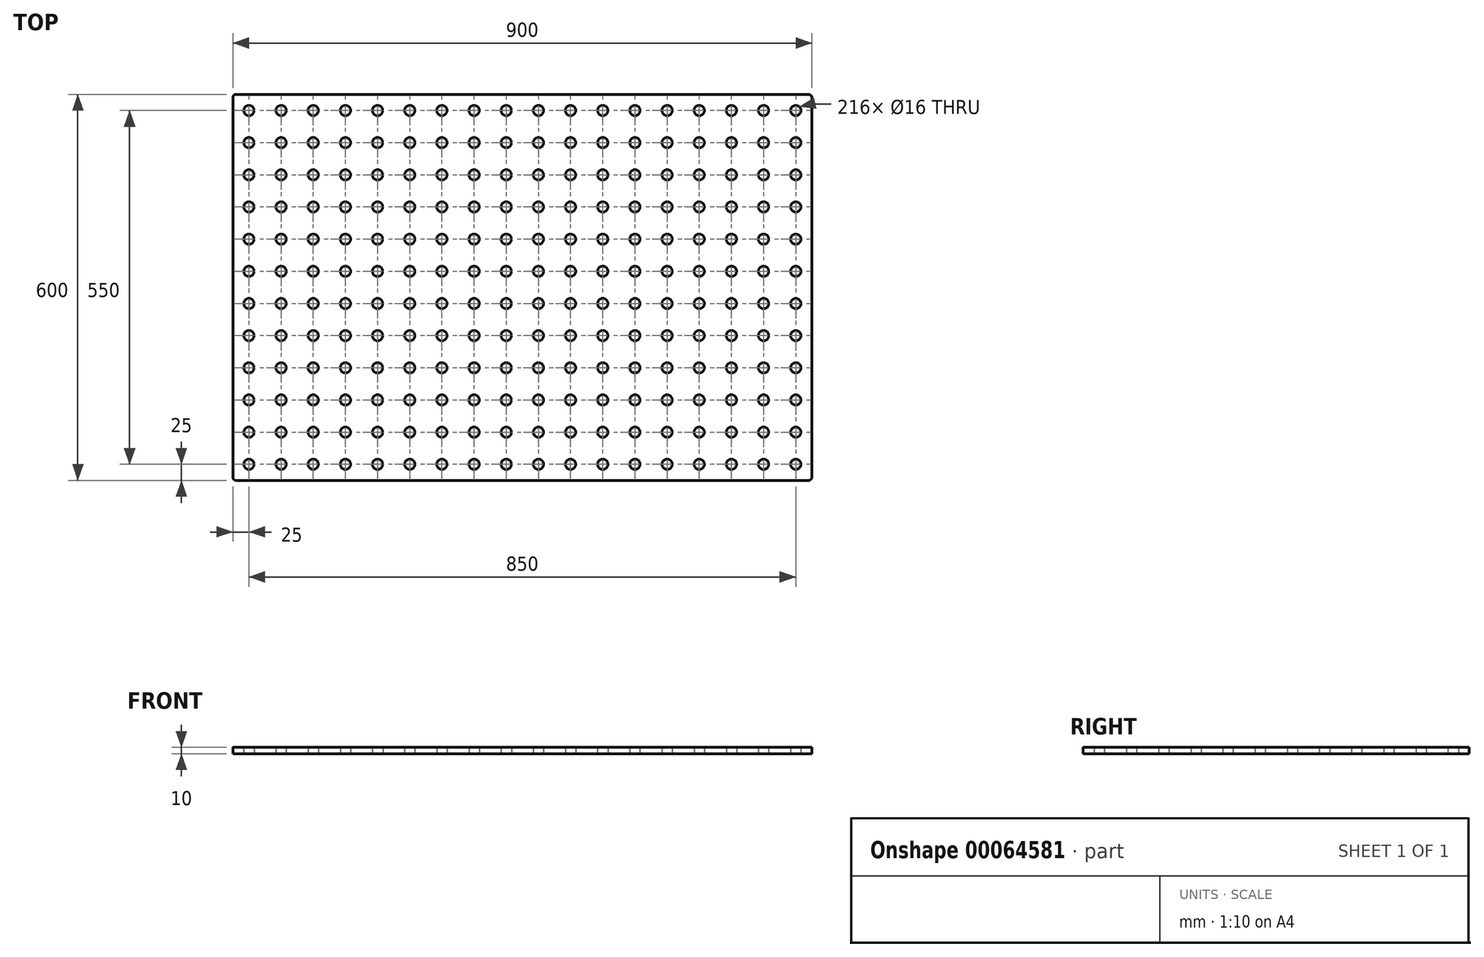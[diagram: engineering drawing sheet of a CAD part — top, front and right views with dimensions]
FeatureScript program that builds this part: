
annotation { "Feature Type Name" : "Feature", "Feature Type Description" : "" }
export const myFeature = defineFeature(function(context is Context, id is Id, definition is map)
    precondition{}
    {
        {
            var Q0;
            Q0=qCreatedBy(makeId("Top.planeOp"),FACE);
            var sketch = newSketch(context, id + "F0", { "sketchPlane" : qUnion([Q0])});
            skLineSegment(sketch, "E0.bottom", {"start": v(5, 0) * mm, "end": v(895, 0) * mm});
            skLineSegment(sketch, "E0.top", {"start": v(5, 600) * mm, "end": v(895, 600) * mm});
            skLineSegment(sketch, "E0.left", {"start": v(0, 5) * mm, "end": v(0, 595) * mm});
            skLineSegment(sketch, "E0.right", {"start": v(900, 5) * mm, "end": v(900, 595) * mm});
            skCircle(sketch, "E1", {"center": v(25, 575) * mm, "radius": 8 * mm});
            skCircle(sketch, "E2.0.1.0", {"center": v(25, 525) * mm, "radius": 8 * mm});
            skCircle(sketch, "E2.0.2.0", {"center": v(25, 475) * mm, "radius": 8 * mm});
            skCircle(sketch, "E2.0.3.0", {"center": v(25, 425) * mm, "radius": 8 * mm});
            skCircle(sketch, "E2.0.4.0", {"center": v(25, 375) * mm, "radius": 8 * mm});
            skCircle(sketch, "E2.0.5.0", {"center": v(25, 325) * mm, "radius": 8 * mm});
            skCircle(sketch, "E2.0.6.0", {"center": v(25, 275) * mm, "radius": 8 * mm});
            skCircle(sketch, "E2.0.7.0", {"center": v(25, 225) * mm, "radius": 8 * mm});
            skCircle(sketch, "E2.0.8.0", {"center": v(25, 175) * mm, "radius": 8 * mm});
            skCircle(sketch, "E2.0.9.0", {"center": v(25, 125) * mm, "radius": 8 * mm});
            skCircle(sketch, "E2.0.10.0", {"center": v(25, 75) * mm, "radius": 8 * mm});
            skCircle(sketch, "E2.0.11.0", {"center": v(25, 25) * mm, "radius": 8 * mm});
            skCircle(sketch, "E2.1.0.0", {"center": v(75, 575) * mm, "radius": 8 * mm});
            skCircle(sketch, "E2.1.1.0", {"center": v(75, 525) * mm, "radius": 8 * mm});
            skCircle(sketch, "E2.1.2.0", {"center": v(75, 475) * mm, "radius": 8 * mm});
            skCircle(sketch, "E2.1.3.0", {"center": v(75, 425) * mm, "radius": 8 * mm});
            skCircle(sketch, "E2.1.4.0", {"center": v(75, 375) * mm, "radius": 8 * mm});
            skCircle(sketch, "E2.1.5.0", {"center": v(75, 325) * mm, "radius": 8 * mm});
            skCircle(sketch, "E2.1.6.0", {"center": v(75, 275) * mm, "radius": 8 * mm});
            skCircle(sketch, "E2.1.7.0", {"center": v(75, 225) * mm, "radius": 8 * mm});
            skCircle(sketch, "E2.1.8.0", {"center": v(75, 175) * mm, "radius": 8 * mm});
            skCircle(sketch, "E2.1.9.0", {"center": v(75, 125) * mm, "radius": 8 * mm});
            skCircle(sketch, "E2.1.10.0", {"center": v(75, 75) * mm, "radius": 8 * mm});
            skCircle(sketch, "E2.1.11.0", {"center": v(75, 25) * mm, "radius": 8 * mm});
            skCircle(sketch, "E2.2.0.0", {"center": v(125, 575) * mm, "radius": 8 * mm});
            skCircle(sketch, "E2.2.1.0", {"center": v(125, 525) * mm, "radius": 8 * mm});
            skCircle(sketch, "E2.2.2.0", {"center": v(125, 475) * mm, "radius": 8 * mm});
            skCircle(sketch, "E2.2.3.0", {"center": v(125, 425) * mm, "radius": 8 * mm});
            skCircle(sketch, "E2.2.4.0", {"center": v(125, 375) * mm, "radius": 8 * mm});
            skCircle(sketch, "E2.2.5.0", {"center": v(125, 325) * mm, "radius": 8 * mm});
            skCircle(sketch, "E2.2.6.0", {"center": v(125, 275) * mm, "radius": 8 * mm});
            skCircle(sketch, "E2.2.7.0", {"center": v(125, 225) * mm, "radius": 8 * mm});
            skCircle(sketch, "E2.2.8.0", {"center": v(125, 175) * mm, "radius": 8 * mm});
            skCircle(sketch, "E2.2.9.0", {"center": v(125, 125) * mm, "radius": 8 * mm});
            skCircle(sketch, "E2.2.10.0", {"center": v(125, 75) * mm, "radius": 8 * mm});
            skCircle(sketch, "E2.2.11.0", {"center": v(125, 25) * mm, "radius": 8 * mm});
            skCircle(sketch, "E2.3.0.0", {"center": v(175, 575) * mm, "radius": 8 * mm});
            skCircle(sketch, "E2.3.1.0", {"center": v(175, 525) * mm, "radius": 8 * mm});
            skCircle(sketch, "E2.3.2.0", {"center": v(175, 475) * mm, "radius": 8 * mm});
            skCircle(sketch, "E2.3.3.0", {"center": v(175, 425) * mm, "radius": 8 * mm});
            skCircle(sketch, "E2.3.4.0", {"center": v(175, 375) * mm, "radius": 8 * mm});
            skCircle(sketch, "E2.3.5.0", {"center": v(175, 325) * mm, "radius": 8 * mm});
            skCircle(sketch, "E2.3.6.0", {"center": v(175, 275) * mm, "radius": 8 * mm});
            skCircle(sketch, "E2.3.7.0", {"center": v(175, 225) * mm, "radius": 8 * mm});
            skCircle(sketch, "E2.3.8.0", {"center": v(175, 175) * mm, "radius": 8 * mm});
            skCircle(sketch, "E2.3.9.0", {"center": v(175, 125) * mm, "radius": 8 * mm});
            skCircle(sketch, "E2.3.10.0", {"center": v(175, 75) * mm, "radius": 8 * mm});
            skCircle(sketch, "E2.3.11.0", {"center": v(175, 25) * mm, "radius": 8 * mm});
            skCircle(sketch, "E2.4.0.0", {"center": v(225, 575) * mm, "radius": 8 * mm});
            skCircle(sketch, "E2.4.1.0", {"center": v(225, 525) * mm, "radius": 8 * mm});
            skCircle(sketch, "E2.4.2.0", {"center": v(225, 475) * mm, "radius": 8 * mm});
            skCircle(sketch, "E2.4.3.0", {"center": v(225, 425) * mm, "radius": 8 * mm});
            skCircle(sketch, "E2.4.4.0", {"center": v(225, 375) * mm, "radius": 8 * mm});
            skCircle(sketch, "E2.4.5.0", {"center": v(225, 325) * mm, "radius": 8 * mm});
            skCircle(sketch, "E2.4.6.0", {"center": v(225, 275) * mm, "radius": 8 * mm});
            skCircle(sketch, "E2.4.7.0", {"center": v(225, 225) * mm, "radius": 8 * mm});
            skCircle(sketch, "E2.4.8.0", {"center": v(225, 175) * mm, "radius": 8 * mm});
            skCircle(sketch, "E2.4.9.0", {"center": v(225, 125) * mm, "radius": 8 * mm});
            skCircle(sketch, "E2.4.10.0", {"center": v(225, 75) * mm, "radius": 8 * mm});
            skCircle(sketch, "E2.4.11.0", {"center": v(225, 25) * mm, "radius": 8 * mm});
            skCircle(sketch, "E2.5.0.0", {"center": v(275, 575) * mm, "radius": 8 * mm});
            skCircle(sketch, "E2.5.1.0", {"center": v(275, 525) * mm, "radius": 8 * mm});
            skCircle(sketch, "E2.5.2.0", {"center": v(275, 475) * mm, "radius": 8 * mm});
            skCircle(sketch, "E2.5.3.0", {"center": v(275, 425) * mm, "radius": 8 * mm});
            skCircle(sketch, "E2.5.4.0", {"center": v(275, 375) * mm, "radius": 8 * mm});
            skCircle(sketch, "E2.5.5.0", {"center": v(275, 325) * mm, "radius": 8 * mm});
            skCircle(sketch, "E2.5.6.0", {"center": v(275, 275) * mm, "radius": 8 * mm});
            skCircle(sketch, "E2.5.7.0", {"center": v(275, 225) * mm, "radius": 8 * mm});
            skCircle(sketch, "E2.5.8.0", {"center": v(275, 175) * mm, "radius": 8 * mm});
            skCircle(sketch, "E2.5.9.0", {"center": v(275, 125) * mm, "radius": 8 * mm});
            skCircle(sketch, "E2.5.10.0", {"center": v(275, 75) * mm, "radius": 8 * mm});
            skCircle(sketch, "E2.5.11.0", {"center": v(275, 25) * mm, "radius": 8 * mm});
            skCircle(sketch, "E2.6.0.0", {"center": v(325, 575) * mm, "radius": 8 * mm});
            skCircle(sketch, "E2.6.1.0", {"center": v(325, 525) * mm, "radius": 8 * mm});
            skCircle(sketch, "E2.6.2.0", {"center": v(325, 475) * mm, "radius": 8 * mm});
            skCircle(sketch, "E2.6.3.0", {"center": v(325, 425) * mm, "radius": 8 * mm});
            skCircle(sketch, "E2.6.4.0", {"center": v(325, 375) * mm, "radius": 8 * mm});
            skCircle(sketch, "E2.6.5.0", {"center": v(325, 325) * mm, "radius": 8 * mm});
            skCircle(sketch, "E2.6.6.0", {"center": v(325, 275) * mm, "radius": 8 * mm});
            skCircle(sketch, "E2.6.7.0", {"center": v(325, 225) * mm, "radius": 8 * mm});
            skCircle(sketch, "E2.6.8.0", {"center": v(325, 175) * mm, "radius": 8 * mm});
            skCircle(sketch, "E2.6.9.0", {"center": v(325, 125) * mm, "radius": 8 * mm});
            skCircle(sketch, "E2.6.10.0", {"center": v(325, 75) * mm, "radius": 8 * mm});
            skCircle(sketch, "E2.6.11.0", {"center": v(325, 25) * mm, "radius": 8 * mm});
            skCircle(sketch, "E2.7.0.0", {"center": v(375, 575) * mm, "radius": 8 * mm});
            skCircle(sketch, "E2.7.1.0", {"center": v(375, 525) * mm, "radius": 8 * mm});
            skCircle(sketch, "E2.7.2.0", {"center": v(375, 475) * mm, "radius": 8 * mm});
            skCircle(sketch, "E2.7.3.0", {"center": v(375, 425) * mm, "radius": 8 * mm});
            skCircle(sketch, "E2.7.4.0", {"center": v(375, 375) * mm, "radius": 8 * mm});
            skCircle(sketch, "E2.7.5.0", {"center": v(375, 325) * mm, "radius": 8 * mm});
            skCircle(sketch, "E2.7.6.0", {"center": v(375, 275) * mm, "radius": 8 * mm});
            skCircle(sketch, "E2.7.7.0", {"center": v(375, 225) * mm, "radius": 8 * mm});
            skCircle(sketch, "E2.7.8.0", {"center": v(375, 175) * mm, "radius": 8 * mm});
            skCircle(sketch, "E2.7.9.0", {"center": v(375, 125) * mm, "radius": 8 * mm});
            skCircle(sketch, "E2.7.10.0", {"center": v(375, 75) * mm, "radius": 8 * mm});
            skCircle(sketch, "E2.7.11.0", {"center": v(375, 25) * mm, "radius": 8 * mm});
            skCircle(sketch, "E2.8.0.0", {"center": v(425, 575) * mm, "radius": 8 * mm});
            skCircle(sketch, "E2.8.1.0", {"center": v(425, 525) * mm, "radius": 8 * mm});
            skCircle(sketch, "E2.8.2.0", {"center": v(425, 475) * mm, "radius": 8 * mm});
            skCircle(sketch, "E2.8.3.0", {"center": v(425, 425) * mm, "radius": 8 * mm});
            skCircle(sketch, "E2.8.4.0", {"center": v(425, 375) * mm, "radius": 8 * mm});
            skCircle(sketch, "E2.8.5.0", {"center": v(425, 325) * mm, "radius": 8 * mm});
            skCircle(sketch, "E2.8.6.0", {"center": v(425, 275) * mm, "radius": 8 * mm});
            skCircle(sketch, "E2.8.7.0", {"center": v(425, 225) * mm, "radius": 8 * mm});
            skCircle(sketch, "E2.8.8.0", {"center": v(425, 175) * mm, "radius": 8 * mm});
            skCircle(sketch, "E2.8.9.0", {"center": v(425, 125) * mm, "radius": 8 * mm});
            skCircle(sketch, "E2.8.10.0", {"center": v(425, 75) * mm, "radius": 8 * mm});
            skCircle(sketch, "E2.8.11.0", {"center": v(425, 25) * mm, "radius": 8 * mm});
            skCircle(sketch, "E2.9.0.0", {"center": v(475, 575) * mm, "radius": 8 * mm});
            skCircle(sketch, "E2.9.1.0", {"center": v(475, 525) * mm, "radius": 8 * mm});
            skCircle(sketch, "E2.9.2.0", {"center": v(475, 475) * mm, "radius": 8 * mm});
            skCircle(sketch, "E2.9.3.0", {"center": v(475, 425) * mm, "radius": 8 * mm});
            skCircle(sketch, "E2.9.4.0", {"center": v(475, 375) * mm, "radius": 8 * mm});
            skCircle(sketch, "E2.9.5.0", {"center": v(475, 325) * mm, "radius": 8 * mm});
            skCircle(sketch, "E2.9.6.0", {"center": v(475, 275) * mm, "radius": 8 * mm});
            skCircle(sketch, "E2.9.7.0", {"center": v(475, 225) * mm, "radius": 8 * mm});
            skCircle(sketch, "E2.9.8.0", {"center": v(475, 175) * mm, "radius": 8 * mm});
            skCircle(sketch, "E2.9.9.0", {"center": v(475, 125) * mm, "radius": 8 * mm});
            skCircle(sketch, "E2.9.10.0", {"center": v(475, 75) * mm, "radius": 8 * mm});
            skCircle(sketch, "E2.9.11.0", {"center": v(475, 25) * mm, "radius": 8 * mm});
            skCircle(sketch, "E2.10.0.0", {"center": v(525, 575) * mm, "radius": 8 * mm});
            skCircle(sketch, "E2.10.1.0", {"center": v(525, 525) * mm, "radius": 8 * mm});
            skCircle(sketch, "E2.10.2.0", {"center": v(525, 475) * mm, "radius": 8 * mm});
            skCircle(sketch, "E2.10.3.0", {"center": v(525, 425) * mm, "radius": 8 * mm});
            skCircle(sketch, "E2.10.4.0", {"center": v(525, 375) * mm, "radius": 8 * mm});
            skCircle(sketch, "E2.10.5.0", {"center": v(525, 325) * mm, "radius": 8 * mm});
            skCircle(sketch, "E2.10.6.0", {"center": v(525, 275) * mm, "radius": 8 * mm});
            skCircle(sketch, "E2.10.7.0", {"center": v(525, 225) * mm, "radius": 8 * mm});
            skCircle(sketch, "E2.10.8.0", {"center": v(525, 175) * mm, "radius": 8 * mm});
            skCircle(sketch, "E2.10.9.0", {"center": v(525, 125) * mm, "radius": 8 * mm});
            skCircle(sketch, "E2.10.10.0", {"center": v(525, 75) * mm, "radius": 8 * mm});
            skCircle(sketch, "E2.10.11.0", {"center": v(525, 25) * mm, "radius": 8 * mm});
            skCircle(sketch, "E2.11.0.0", {"center": v(575, 575) * mm, "radius": 8 * mm});
            skCircle(sketch, "E2.11.1.0", {"center": v(575, 525) * mm, "radius": 8 * mm});
            skCircle(sketch, "E2.11.2.0", {"center": v(575, 475) * mm, "radius": 8 * mm});
            skCircle(sketch, "E2.11.3.0", {"center": v(575, 425) * mm, "radius": 8 * mm});
            skCircle(sketch, "E2.11.4.0", {"center": v(575, 375) * mm, "radius": 8 * mm});
            skCircle(sketch, "E2.11.5.0", {"center": v(575, 325) * mm, "radius": 8 * mm});
            skCircle(sketch, "E2.11.6.0", {"center": v(575, 275) * mm, "radius": 8 * mm});
            skCircle(sketch, "E2.11.7.0", {"center": v(575, 225) * mm, "radius": 8 * mm});
            skCircle(sketch, "E2.11.8.0", {"center": v(575, 175) * mm, "radius": 8 * mm});
            skCircle(sketch, "E2.11.9.0", {"center": v(575, 125) * mm, "radius": 8 * mm});
            skCircle(sketch, "E2.11.10.0", {"center": v(575, 75) * mm, "radius": 8 * mm});
            skCircle(sketch, "E2.11.11.0", {"center": v(575, 25) * mm, "radius": 8 * mm});
            skCircle(sketch, "E2.12.0.0", {"center": v(625, 575) * mm, "radius": 8 * mm});
            skCircle(sketch, "E2.12.1.0", {"center": v(625, 525) * mm, "radius": 8 * mm});
            skCircle(sketch, "E2.12.2.0", {"center": v(625, 475) * mm, "radius": 8 * mm});
            skCircle(sketch, "E2.12.3.0", {"center": v(625, 425) * mm, "radius": 8 * mm});
            skCircle(sketch, "E2.12.4.0", {"center": v(625, 375) * mm, "radius": 8 * mm});
            skCircle(sketch, "E2.12.5.0", {"center": v(625, 325) * mm, "radius": 8 * mm});
            skCircle(sketch, "E2.12.6.0", {"center": v(625, 275) * mm, "radius": 8 * mm});
            skCircle(sketch, "E2.12.7.0", {"center": v(625, 225) * mm, "radius": 8 * mm});
            skCircle(sketch, "E2.12.8.0", {"center": v(625, 175) * mm, "radius": 8 * mm});
            skCircle(sketch, "E2.12.9.0", {"center": v(625, 125) * mm, "radius": 8 * mm});
            skCircle(sketch, "E2.12.10.0", {"center": v(625, 75) * mm, "radius": 8 * mm});
            skCircle(sketch, "E2.12.11.0", {"center": v(625, 25) * mm, "radius": 8 * mm});
            skCircle(sketch, "E2.13.0.0", {"center": v(675, 575) * mm, "radius": 8 * mm});
            skCircle(sketch, "E2.13.1.0", {"center": v(675, 525) * mm, "radius": 8 * mm});
            skCircle(sketch, "E2.13.2.0", {"center": v(675, 475) * mm, "radius": 8 * mm});
            skCircle(sketch, "E2.13.3.0", {"center": v(675, 425) * mm, "radius": 8 * mm});
            skCircle(sketch, "E2.13.4.0", {"center": v(675, 375) * mm, "radius": 8 * mm});
            skCircle(sketch, "E2.13.5.0", {"center": v(675, 325) * mm, "radius": 8 * mm});
            skCircle(sketch, "E2.13.6.0", {"center": v(675, 275) * mm, "radius": 8 * mm});
            skCircle(sketch, "E2.13.7.0", {"center": v(675, 225) * mm, "radius": 8 * mm});
            skCircle(sketch, "E2.13.8.0", {"center": v(675, 175) * mm, "radius": 8 * mm});
            skCircle(sketch, "E2.13.9.0", {"center": v(675, 125) * mm, "radius": 8 * mm});
            skCircle(sketch, "E2.13.10.0", {"center": v(675, 75) * mm, "radius": 8 * mm});
            skCircle(sketch, "E2.13.11.0", {"center": v(675, 25) * mm, "radius": 8 * mm});
            skCircle(sketch, "E2.14.0.0", {"center": v(725, 575) * mm, "radius": 8 * mm});
            skCircle(sketch, "E2.14.1.0", {"center": v(725, 525) * mm, "radius": 8 * mm});
            skCircle(sketch, "E2.14.2.0", {"center": v(725, 475) * mm, "radius": 8 * mm});
            skCircle(sketch, "E2.14.3.0", {"center": v(725, 425) * mm, "radius": 8 * mm});
            skCircle(sketch, "E2.14.4.0", {"center": v(725, 375) * mm, "radius": 8 * mm});
            skCircle(sketch, "E2.14.5.0", {"center": v(725, 325) * mm, "radius": 8 * mm});
            skCircle(sketch, "E2.14.6.0", {"center": v(725, 275) * mm, "radius": 8 * mm});
            skCircle(sketch, "E2.14.7.0", {"center": v(725, 225) * mm, "radius": 8 * mm});
            skCircle(sketch, "E2.14.8.0", {"center": v(725, 175) * mm, "radius": 8 * mm});
            skCircle(sketch, "E2.14.9.0", {"center": v(725, 125) * mm, "radius": 8 * mm});
            skCircle(sketch, "E2.14.10.0", {"center": v(725, 75) * mm, "radius": 8 * mm});
            skCircle(sketch, "E2.14.11.0", {"center": v(725, 25) * mm, "radius": 8 * mm});
            skCircle(sketch, "E2.15.0.0", {"center": v(775, 575) * mm, "radius": 8 * mm});
            skCircle(sketch, "E2.15.1.0", {"center": v(775, 525) * mm, "radius": 8 * mm});
            skCircle(sketch, "E2.15.2.0", {"center": v(775, 475) * mm, "radius": 8 * mm});
            skCircle(sketch, "E2.15.3.0", {"center": v(775, 425) * mm, "radius": 8 * mm});
            skCircle(sketch, "E2.15.4.0", {"center": v(775, 375) * mm, "radius": 8 * mm});
            skCircle(sketch, "E2.15.5.0", {"center": v(775, 325) * mm, "radius": 8 * mm});
            skCircle(sketch, "E2.15.6.0", {"center": v(775, 275) * mm, "radius": 8 * mm});
            skCircle(sketch, "E2.15.7.0", {"center": v(775, 225) * mm, "radius": 8 * mm});
            skCircle(sketch, "E2.15.8.0", {"center": v(775, 175) * mm, "radius": 8 * mm});
            skCircle(sketch, "E2.15.9.0", {"center": v(775, 125) * mm, "radius": 8 * mm});
            skCircle(sketch, "E2.15.10.0", {"center": v(775, 75) * mm, "radius": 8 * mm});
            skCircle(sketch, "E2.15.11.0", {"center": v(775, 25) * mm, "radius": 8 * mm});
            skCircle(sketch, "E2.16.0.0", {"center": v(825, 575) * mm, "radius": 8 * mm});
            skCircle(sketch, "E2.16.1.0", {"center": v(825, 525) * mm, "radius": 8 * mm});
            skCircle(sketch, "E2.16.2.0", {"center": v(825, 475) * mm, "radius": 8 * mm});
            skCircle(sketch, "E2.16.3.0", {"center": v(825, 425) * mm, "radius": 8 * mm});
            skCircle(sketch, "E2.16.4.0", {"center": v(825, 375) * mm, "radius": 8 * mm});
            skCircle(sketch, "E2.16.5.0", {"center": v(825, 325) * mm, "radius": 8 * mm});
            skCircle(sketch, "E2.16.6.0", {"center": v(825, 275) * mm, "radius": 8 * mm});
            skCircle(sketch, "E2.16.7.0", {"center": v(825, 225) * mm, "radius": 8 * mm});
            skCircle(sketch, "E2.16.8.0", {"center": v(825, 175) * mm, "radius": 8 * mm});
            skCircle(sketch, "E2.16.9.0", {"center": v(825, 125) * mm, "radius": 8 * mm});
            skCircle(sketch, "E2.16.10.0", {"center": v(825, 75) * mm, "radius": 8 * mm});
            skCircle(sketch, "E2.16.11.0", {"center": v(825, 25) * mm, "radius": 8 * mm});
            skCircle(sketch, "E2.17.0.0", {"center": v(875, 575) * mm, "radius": 8 * mm});
            skCircle(sketch, "E2.17.1.0", {"center": v(875, 525) * mm, "radius": 8 * mm});
            skCircle(sketch, "E2.17.2.0", {"center": v(875, 475) * mm, "radius": 8 * mm});
            skCircle(sketch, "E2.17.3.0", {"center": v(875, 425) * mm, "radius": 8 * mm});
            skCircle(sketch, "E2.17.4.0", {"center": v(875, 375) * mm, "radius": 8 * mm});
            skCircle(sketch, "E2.17.5.0", {"center": v(875, 325) * mm, "radius": 8 * mm});
            skCircle(sketch, "E2.17.6.0", {"center": v(875, 275) * mm, "radius": 8 * mm});
            skCircle(sketch, "E2.17.7.0", {"center": v(875, 225) * mm, "radius": 8 * mm});
            skCircle(sketch, "E2.17.8.0", {"center": v(875, 175) * mm, "radius": 8 * mm});
            skCircle(sketch, "E2.17.9.0", {"center": v(875, 125) * mm, "radius": 8 * mm});
            skCircle(sketch, "E2.17.10.0", {"center": v(875, 75) * mm, "radius": 8 * mm});
            skCircle(sketch, "E2.17.11.0", {"center": v(875, 25) * mm, "radius": 8 * mm});
            skLineSegment(sketch, "E2.direction1", {"start": v(25, 575) * mm, "end": v(75, 575) * mm, "construction": true});
            skLineSegment(sketch, "E2.direction2", {"start": v(25, 575) * mm, "end": v(25, 525) * mm, "construction": true});
            skPoint(sketch, "E3.visualSharp", {"position": v(900, 600) * mm});
            skArc(sketch, "E3.filletArc", {"start": v(900, 595) * mm, "mid": v(898.54, 598.54) * mm, "end": v(895, 600) * mm});
            skPoint(sketch, "E4.visualSharp", {"position": v(900, 0) * mm});
            skArc(sketch, "E4.filletArc", {"start": v(895, 0) * mm, "mid": v(898.54, 1.46) * mm, "end": v(900, 5) * mm});
            skPoint(sketch, "E5.visualSharp", {"position": v(0, 0) * mm});
            skArc(sketch, "E5.filletArc", {"start": v(0, 5) * mm, "mid": v(1.46, 1.46) * mm, "end": v(5, 0) * mm});
            skPoint(sketch, "E6.visualSharp", {"position": v(0, 600) * mm});
            skArc(sketch, "E6.filletArc", {"start": v(5, 600) * mm, "mid": v(1.46, 598.54) * mm, "end": v(0, 595) * mm});
            skSolve(sketch);
        }
        {
            var Q0;
            Q0 = qSketchRegion(id + "F0", true);
            extrude(context, id + "F1", {"entities" : qUnion([Q0]), "depth" : 10 * mm});
        }
    });
